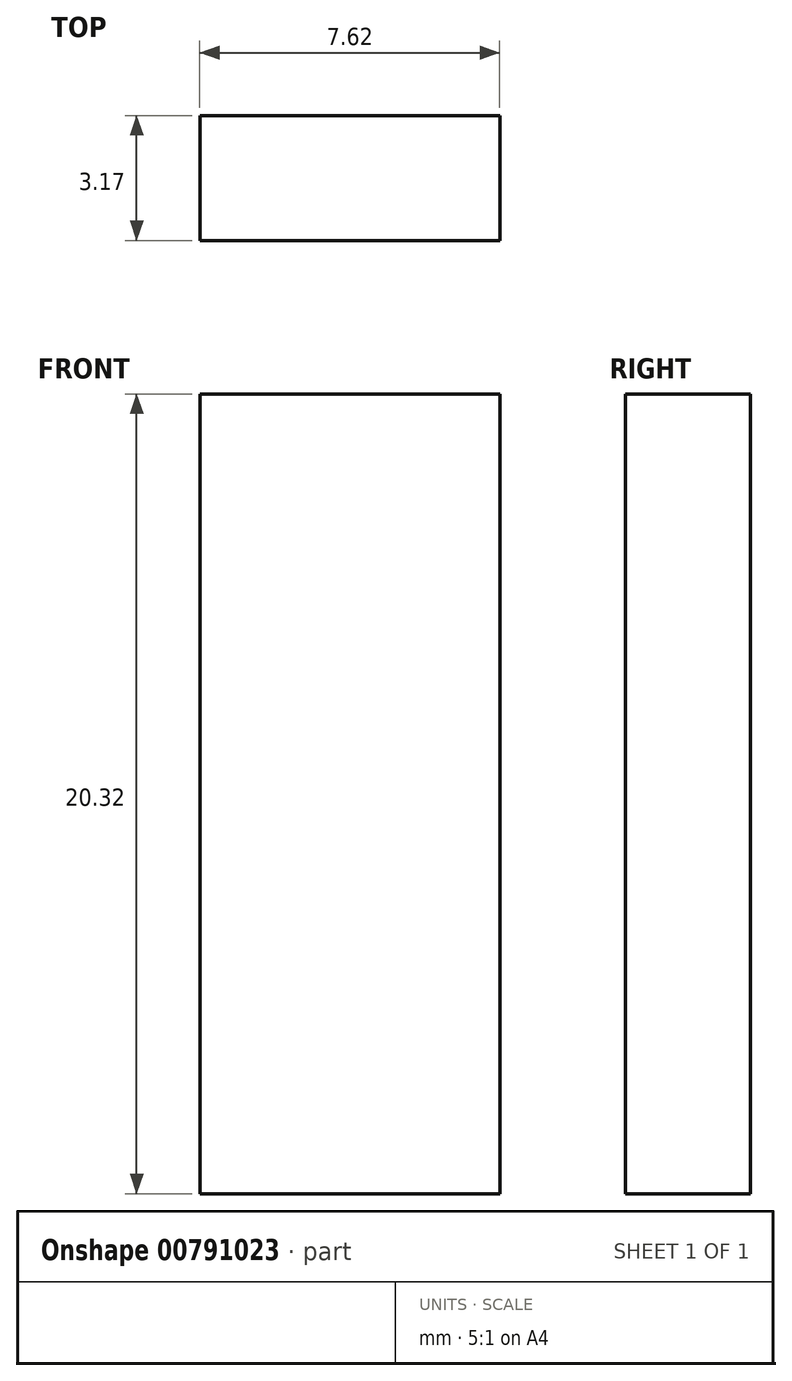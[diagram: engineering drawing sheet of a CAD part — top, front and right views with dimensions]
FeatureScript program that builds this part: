
annotation { "Feature Type Name" : "Feature", "Feature Type Description" : "" }
export const myFeature = defineFeature(function(context is Context, id is Id, definition is map)
    precondition{}
    {
        {
            var Q0;
            Q0=qCreatedBy(makeId("Front.planeOp"),FACE);
            var sketch = newSketch(context, id + "F0", { "sketchPlane" : qUnion([Q0])});
            skLineSegment(sketch, "E0.bottom", {"start": v(-13.89, 7.54) * mm, "end": v(-6.27, 7.54) * mm});
            skLineSegment(sketch, "E0.top", {"start": v(-13.89, -12.78) * mm, "end": v(-6.27, -12.78) * mm});
            skLineSegment(sketch, "E0.left", {"start": v(-13.89, 7.54) * mm, "end": v(-13.89, -12.78) * mm});
            skLineSegment(sketch, "E0.right", {"start": v(-6.27, 7.54) * mm, "end": v(-6.27, -12.78) * mm});
            skSolve(sketch);
        }
        {
            var Q0;
            Q0 = qSketchRegion(id + "F0", true);
            extrude(context, id + "F1", {"entities" : qUnion([Q0]), "depth" : 3.17 * mm, "offsetDistance" : 25.4 * mm});
        }
    });
